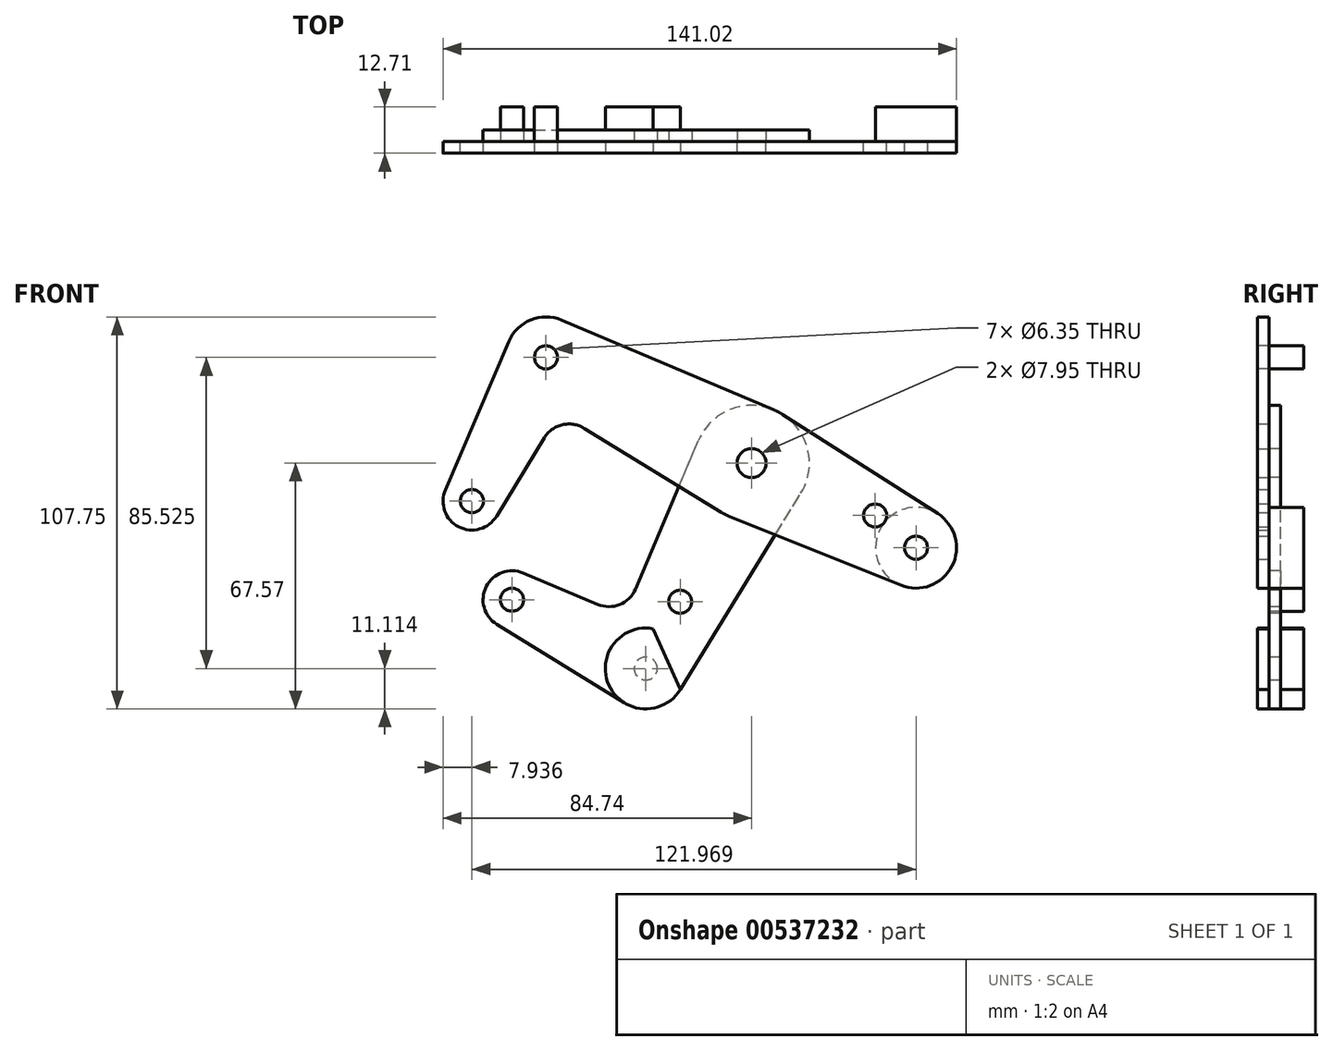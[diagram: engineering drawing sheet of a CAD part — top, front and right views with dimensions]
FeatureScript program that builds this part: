
annotation { "Feature Type Name" : "Feature", "Feature Type Description" : "" }
export const myFeature = defineFeature(function(context is Context, id is Id, definition is map)
    precondition{}
    {
        {
            var Q0;
            Q0=qCreatedBy(makeId("Front.planeOp"),FACE);
            var sketch = newSketch(context, id + "F0", { "sketchPlane" : qUnion([Q0])});
            skCircle(sketch, "E0", {"center": v(0, 0) * mm, "radius": 0.63 * mm});
            skCircle(sketch, "E1", {"center": v(0, 0) * mm, "radius": 15.88 * mm});
            skCircle(sketch, "E2", {"center": v(0, 0) * mm, "radius": 3.98 * mm});
            skCircle(sketch, "E3", {"center": v(45.16, -23.25) * mm, "radius": 11.11 * mm});
            skCircle(sketch, "E4", {"center": v(45.16, -23.25) * mm, "radius": 3.18 * mm});
            skLineSegment(sketch, "E5", {"start": v(-5.91, -14.73) * mm, "end": v(41.03, -33.57) * mm});
            skLineSegment(sketch, "E6", {"start": v(51.16, -13.9) * mm, "end": v(8.56, 13.37) * mm});
            skCircle(sketch, "E7", {"center": v(33.95, -14.4) * mm, "radius": 3.18 * mm});
            skCircle(sketch, "E8", {"center": v(-56.46, 29.07) * mm, "radius": 11.11 * mm});
            skCircle(sketch, "E9", {"center": v(-56.46, 29.07) * mm, "radius": 3.18 * mm});
            skLineSegment(sketch, "E10", {"start": v(-52.12, 39.3) * mm, "end": v(6.19, 14.62) * mm});
            skLineSegment(sketch, "E11", {"start": v(45.16, -23.25) * mm, "end": v(0, 0) * mm, "construction": true});
            skLineSegment(sketch, "E12", {"start": v(0, 0) * mm, "end": v(-56.46, 29.07) * mm, "construction": true});
            skLineSegment(sketch, "E13", {"start": v(-56.46, 29.07) * mm, "end": v(-76.8, -10.45) * mm, "construction": true});
            skCircle(sketch, "E14", {"center": v(-76.8, -10.45) * mm, "radius": 7.94 * mm});
            skCircle(sketch, "E15", {"center": v(-76.8, -10.45) * mm, "radius": 3.18 * mm});
            skLineSegment(sketch, "E16", {"start": v(-84.1, -7.33) * mm, "end": v(-66.67, 33.44) * mm});
            skLineSegment(sketch, "E17", {"start": v(-70.02, -14.58) * mm, "end": v(-56.91, 6.95) * mm});
            skLineSegment(sketch, "E18", {"start": v(-8.3, -13.53) * mm, "end": v(-45.97, 9.59) * mm});
            skArc(sketch, "E19.filletArc", {"start": v(-45.97, 9.59) * mm, "mid": v(-51.99, 10.54) * mm, "end": v(-56.91, 6.95) * mm});
            skLineSegment(sketch, "E20", {"start": v(0, 0) * mm, "end": v(-29.07, -56.46) * mm, "construction": true});
            skCircle(sketch, "E21", {"center": v(-29.07, -56.46) * mm, "radius": 11.11 * mm});
            skCircle(sketch, "E22", {"center": v(-19.62, -38.1) * mm, "radius": 3.18 * mm});
            skCircle(sketch, "E23", {"center": v(-29.07, -56.46) * mm, "radius": 3.18 * mm});
            skLineSegment(sketch, "E24", {"start": v(-19.6, -62.27) * mm, "end": v(13.53, -8.3) * mm});
            skLineSegment(sketch, "E25", {"start": v(-29.07, -56.46) * mm, "end": v(-65.8, -37.54) * mm, "construction": true});
            skCircle(sketch, "E26", {"center": v(-65.8, -37.54) * mm, "radius": 7.94 * mm});
            skCircle(sketch, "E27", {"center": v(-65.8, -37.54) * mm, "radius": 3.18 * mm});
            skLineSegment(sketch, "E28", {"start": v(-34.9, -65.92) * mm, "end": v(-69.97, -44.3) * mm});
            skLineSegment(sketch, "E29", {"start": v(-62.73, -30.22) * mm, "end": v(-42.3, -38.83) * mm});
            skLineSegment(sketch, "E30", {"start": v(-31.89, -34.6) * mm, "end": v(-14.15, 7.29) * mm});
            skArc(sketch, "E31.filletArc", {"start": v(-42.3, -38.83) * mm, "mid": v(-36.21, -38.87) * mm, "end": v(-31.89, -34.6) * mm});
            skSolve(sketch);
        }
        {
            var Q0;
            {var subQ7=sQuery(id+"F0.wireOp",EDGE,"E6");Q0=makeQuery(id+"F0.imprint","IMPRINT",FACE,{"disambiguationData":[TD([[makeQuery(id+"F0.imprint","IMPRINT",EDGE,{"derivedFrom":subQ7}),1.0]])]});}
            var Q1;
            Q1=makeQuery(id+"F0.imprint","IMPRINT",FACE,{"disambiguationData":[TD([[makeQuery(id+"F0.imprint","IMPRINT",EDGE,{"derivedFrom":sQuery(id+"F0.wireOp",EDGE,"E2")}),-1.0]])]});
            var Q2;
            {var subQ0=sQuery(id+"F0.wireOp",EDGE,"E5");var subQ1=sQuery(id+"F0.wireOp",EDGE,"E1");var subQ2=makeQuery(id+"F0.imprint","INTERSECT",VERTEX,{"derivedFrom":[subQ1,subQ0]});Q2=makeQuery(id+"F0.imprint","IMPRINT",FACE,{"disambiguationData":[TD([[makeQuery(id+"F0.imprint","IMPRINT",EDGE,{"disambiguationData":[TD([[subQ2,-1.0]])],"derivedFrom":subQ1}),-1.0]])]});}
            var Q3;
            {var subQ0=sQuery(id+"F0.wireOp",EDGE,"E18");var subQ1=sQuery(id+"F0.wireOp",EDGE,"E1");var subQ2=makeQuery(id+"F0.imprint","INTERSECT",VERTEX,{"derivedFrom":[subQ1,subQ0]});Q3=makeQuery(id+"F0.imprint","IMPRINT",FACE,{"disambiguationData":[TD([[makeQuery(id+"F0.imprint","IMPRINT",EDGE,{"disambiguationData":[TD([[subQ2,1.0]])],"derivedFrom":subQ1}),-1.0]])]});}
            var Q4;
            {var subQ3=sQuery(id+"F0.wireOp",EDGE,"E10");Q4=makeQuery(id+"F0.imprint","IMPRINT",FACE,{"disambiguationData":[TD([[makeQuery(id+"F0.imprint","IMPRINT",EDGE,{"derivedFrom":subQ3}),-1.0]])]});}
            var Q5;
            Q5=makeQuery(id+"F0.imprint","IMPRINT",FACE,{"disambiguationData":[TD([[makeQuery(id+"F0.imprint","IMPRINT",EDGE,{"derivedFrom":sQuery(id+"F0.wireOp",EDGE,"E9")}),-1.0]])]});
            var Q6;
            Q6=makeQuery(id+"F0.imprint","IMPRINT",FACE,{"disambiguationData":[TD([[makeQuery(id+"F0.imprint","IMPRINT",EDGE,{"derivedFrom":sQuery(id+"F0.wireOp",EDGE,"E4")}),-1.0]])]});
            var Q7;
            Q7=makeQuery(id+"F0.imprint","IMPRINT",FACE,{"disambiguationData":[TD([[makeQuery(id+"F0.imprint","IMPRINT",EDGE,{"derivedFrom":sQuery(id+"F0.wireOp",EDGE,"E15")}),-1.0]])]});
            extrude(context, id + "F1", {"entities" : qUnion([Q0, Q1, Q2, Q3, Q4, Q5, Q6, Q7]), "depth" : 3.17 * mm, "offsetDistance" : 25.4 * mm});
        }
        {
            var Q0;
            Q0=makeQuery(id+"F0.imprint","IMPRINT",FACE,{"disambiguationData":[TD([[makeQuery(id+"F0.imprint","IMPRINT",EDGE,{"derivedFrom":sQuery(id+"F0.wireOp",EDGE,"E22")}),-1.0]])]});
            var Q1;
            Q1=makeQuery(id+"F0.imprint","IMPRINT",FACE,{"disambiguationData":[TD([[makeQuery(id+"F0.imprint","IMPRINT",EDGE,{"derivedFrom":sQuery(id+"F0.wireOp",EDGE,"E23")}),-1.0]])]});
            var Q2;
            Q2=makeQuery(id+"F0.imprint","IMPRINT",FACE,{"disambiguationData":[TD([[makeQuery(id+"F0.imprint","IMPRINT",EDGE,{"derivedFrom":sQuery(id+"F0.wireOp",EDGE,"E27")}),-1.0]])]});
            var Q3;
            {var subQ0=sQuery(id+"F0.wireOp",EDGE,"E5");var subQ1=sQuery(id+"F0.wireOp",EDGE,"E1");var subQ2=makeQuery(id+"F0.imprint","INTERSECT",VERTEX,{"derivedFrom":[subQ1,subQ0]});Q3=makeQuery(id+"F0.imprint","IMPRINT",FACE,{"disambiguationData":[TD([[makeQuery(id+"F0.imprint","IMPRINT",EDGE,{"disambiguationData":[TD([[subQ2,-1.0]])],"derivedFrom":subQ1}),-1.0]])]});}
            var Q4;
            {var subQ0=sQuery(id+"F0.wireOp",EDGE,"E18");var subQ1=sQuery(id+"F0.wireOp",EDGE,"E1");var subQ2=makeQuery(id+"F0.imprint","INTERSECT",VERTEX,{"derivedFrom":[subQ1,subQ0]});Q4=makeQuery(id+"F0.imprint","IMPRINT",FACE,{"disambiguationData":[TD([[makeQuery(id+"F0.imprint","IMPRINT",EDGE,{"disambiguationData":[TD([[subQ2,1.0]])],"derivedFrom":subQ1}),-1.0]])]});}
            var Q5;
            Q5=makeQuery(id+"F0.imprint","IMPRINT",FACE,{"disambiguationData":[TD([[makeQuery(id+"F0.imprint","IMPRINT",EDGE,{"derivedFrom":sQuery(id+"F0.wireOp",EDGE,"E2")}),-1.0]])]});
            extrude(context, id + "F2", {"entities" : qUnion([Q0, Q1, Q2, Q3, Q4, Q5]), "oppositeDirection" : true, "depth" : 3.17 * mm, "offsetDistance" : 25.4 * mm});
        }
        {
            var Q0;
            Q0=makeQuery(id+"F1.opExtrude","CAP_FACE",FACE,{"disambiguationData":[OSD([sQuery(id+"F0.wireOp",EDGE,"E1"),sQuery(id+"F0.wireOp",EDGE,"E2"),sQuery(id+"F0.wireOp",EDGE,"E3"),sQuery(id+"F0.wireOp",EDGE,"E4"),sQuery(id+"F0.wireOp",EDGE,"E5"),sQuery(id+"F0.wireOp",EDGE,"E6"),sQuery(id+"F0.wireOp",EDGE,"E7"),sQuery(id+"F0.wireOp",EDGE,"E8"),sQuery(id+"F0.wireOp",EDGE,"E9"),sQuery(id+"F0.wireOp",EDGE,"E10"),sQuery(id+"F0.wireOp",EDGE,"E14"),sQuery(id+"F0.wireOp",EDGE,"E15"),sQuery(id+"F0.wireOp",EDGE,"E16"),sQuery(id+"F0.wireOp",EDGE,"E17"),sQuery(id+"F0.wireOp",EDGE,"E18"),sQuery(id+"F0.wireOp",EDGE,"E19.filletArc")])],"isStart":false});
            var sketch = newSketch(context, id + "F3", { "sketchPlane" : qUnion([Q0])});
            skCircle(sketch, "E32", {"center": v(-56.46, 29.07) * mm, "radius": 3.98 * mm});
            skCircle(sketch, "E33", {"center": v(0, 0) * mm, "radius": 3.98 * mm});
            skCircle(sketch, "E34", {"center": v(45.16, -23.25) * mm, "radius": 11.11 * mm});
            skCircle(sketch, "E35", {"center": v(-29.07, -56.46) * mm, "radius": 11.11 * mm});
            skLineSegment(sketch, "E36", {"start": v(-29.07, -56.46) * mm, "end": v(45.16, -23.25) * mm, "construction": true});
            skLineSegment(sketch, "E37", {"start": v(-29.07, -56.46) * mm, "end": v(-23.27, -53.86) * mm});
            skLineSegment(sketch, "E38", {"start": v(-27, -45.54) * mm, "end": v(-19.55, -62.19) * mm});
            skSolve(sketch);
        }
        {
            var Q0;
            Q0=qCreatedBy(makeId("Front.planeOp"),FACE);
            cPlane(context, id + "F4", {"entities" : qUnion([Q0]), "cplaneType" : CPlaneType.OFFSET, "offset" : 9.52 * mm, "oppositeDirection" : true, "width" : 152.4 * mm, "height" : 152.4 * mm});
        }
        {
            var Q0;
            {var subQ0=sQuery(id+"F3.wireOp",EDGE,"E38");var subQ4=makeQuery(id+"F3.imprint","IMPRINT",VERTEX,{"derivedFrom":subQ0});Q0=makeQuery(id+"F3.imprint","IMPRINT",FACE,{"disambiguationData":[TD([[makeQuery(id+"F3.imprint","IMPRINT",EDGE,{"disambiguationData":[TD([[subQ4,1.0]])],"derivedFrom":subQ0}),-1.0]])]});}
            var Q1;
            Q1=makeQuery(id+"F3.imprint","IMPRINT",FACE,{"disambiguationData":[TD([[makeQuery(id+"F3.imprint","IMPRINT",EDGE,{"derivedFrom":makeQuery(id+"F1.opExtrude","CAP_EDGE",EDGE,{"disambiguationData":[OSD([sQuery(id+"F0.wireOp",EDGE,"E9")])],"isStart":false})}),1.0]])]});
            var Q2;
            Q2=makeQuery(id+"F3.imprint","IMPRINT",FACE,{"disambiguationData":[TD([[makeQuery(id+"F3.imprint","IMPRINT",EDGE,{"derivedFrom":makeQuery(id+"F1.opExtrude","CAP_EDGE",EDGE,{"disambiguationData":[OSD([sQuery(id+"F0.wireOp",EDGE,"E4")])],"isStart":false})}),-1.0]])]});
            var Q3;
            Q3=makeQuery(id+"F0.imprint","IMPRINT",FACE,{"disambiguationData":[TD([[makeQuery(id+"F0.imprint","IMPRINT",EDGE,{"derivedFrom":sQuery(id+"F0.wireOp",EDGE,"E27")}),1.0]])]});
            var Q4;
            Q4=makeQuery(id+"F3.imprint","IMPRINT",FACE,{"disambiguationData":[TD([[makeQuery(id+"F3.imprint","IMPRINT",EDGE,{"derivedFrom":makeQuery(id+"F1.opExtrude","CAP_EDGE",EDGE,{"disambiguationData":[OSD([sQuery(id+"F0.wireOp",EDGE,"E4")])],"isStart":false})}),1.0]])]});
            var Q5;
            Q5=qCreatedBy(id+"F4.planeOp",FACE);
            extrude(context, id + "F5", {"entities" : qUnion([Q0, Q1, Q2, Q3, Q4]), "endBound" : BoundingType.UP_TO_SURFACE, "oppositeDirection" : true, "depth" : 25.4 * mm, "endBoundEntityFace" : qUnion([Q5]), "offsetDistance" : 25.4 * mm});
        }
        {
            var Q0;
            Q0=makeQuery(id+"F1.opExtrude","SWEPT_BODY",BODY,{"disambiguationData":[OSD([sQuery(id+"F0.wireOp",EDGE,"E1"),sQuery(id+"F0.wireOp",EDGE,"E2"),sQuery(id+"F0.wireOp",EDGE,"E3"),sQuery(id+"F0.wireOp",EDGE,"E4"),sQuery(id+"F0.wireOp",EDGE,"E5"),sQuery(id+"F0.wireOp",EDGE,"E6"),sQuery(id+"F0.wireOp",EDGE,"E7"),sQuery(id+"F0.wireOp",EDGE,"E8"),sQuery(id+"F0.wireOp",EDGE,"E9"),sQuery(id+"F0.wireOp",EDGE,"E10"),sQuery(id+"F0.wireOp",EDGE,"E14"),sQuery(id+"F0.wireOp",EDGE,"E15"),sQuery(id+"F0.wireOp",EDGE,"E16"),sQuery(id+"F0.wireOp",EDGE,"E17"),sQuery(id+"F0.wireOp",EDGE,"E18"),sQuery(id+"F0.wireOp",EDGE,"E19.filletArc")])]});
            var Q1;
            Q1=makeQuery(id+"F2.opExtrude","SWEPT_BODY",BODY,{"disambiguationData":[OSD([sQuery(id+"F0.wireOp",EDGE,"E1"),sQuery(id+"F0.wireOp",EDGE,"E2"),sQuery(id+"F0.wireOp",EDGE,"E21"),sQuery(id+"F0.wireOp",EDGE,"E22"),sQuery(id+"F0.wireOp",EDGE,"E23"),sQuery(id+"F0.wireOp",EDGE,"E24"),sQuery(id+"F0.wireOp",EDGE,"E26"),sQuery(id+"F0.wireOp",EDGE,"E27"),sQuery(id+"F0.wireOp",EDGE,"E28"),sQuery(id+"F0.wireOp",EDGE,"E29"),sQuery(id+"F0.wireOp",EDGE,"E30"),sQuery(id+"F0.wireOp",EDGE,"E31.filletArc")])]});
            var Q2;
            Q2=makeQuery(id+"F5.opExtrude","SWEPT_BODY",BODY,{"disambiguationData":[OSD([sQuery(id+"F3.wireOp",EDGE,"E34")])]});
            var Q3;
            Q3=makeQuery(id+"F5.opExtrude","SWEPT_BODY",BODY,{"disambiguationData":[OSD([sQuery(id+"F3.wireOp",EDGE,"E35"),sQuery(id+"F3.wireOp",EDGE,"E38")])]});
            var Q4;
            Q4=makeQuery(id+"F5.opExtrude","SWEPT_BODY",BODY,{"disambiguationData":[OSD([sQuery(id+"F0.wireOp",EDGE,"E9")])]});
            var Q5;
            Q5=makeQuery(id+"F5.opExtrude","SWEPT_BODY",BODY,{"disambiguationData":[OSD([sQuery(id+"F0.wireOp",EDGE,"E27")])]});
            booleanBodies(context, id + "F6", {"operationType" : BooleanOperationType.SUBTRACTION, "tools" : qUnion([Q0, Q1]), "targets" : qUnion([Q2, Q3, Q4, Q5]), "keepTools" : true});
        }
    });
